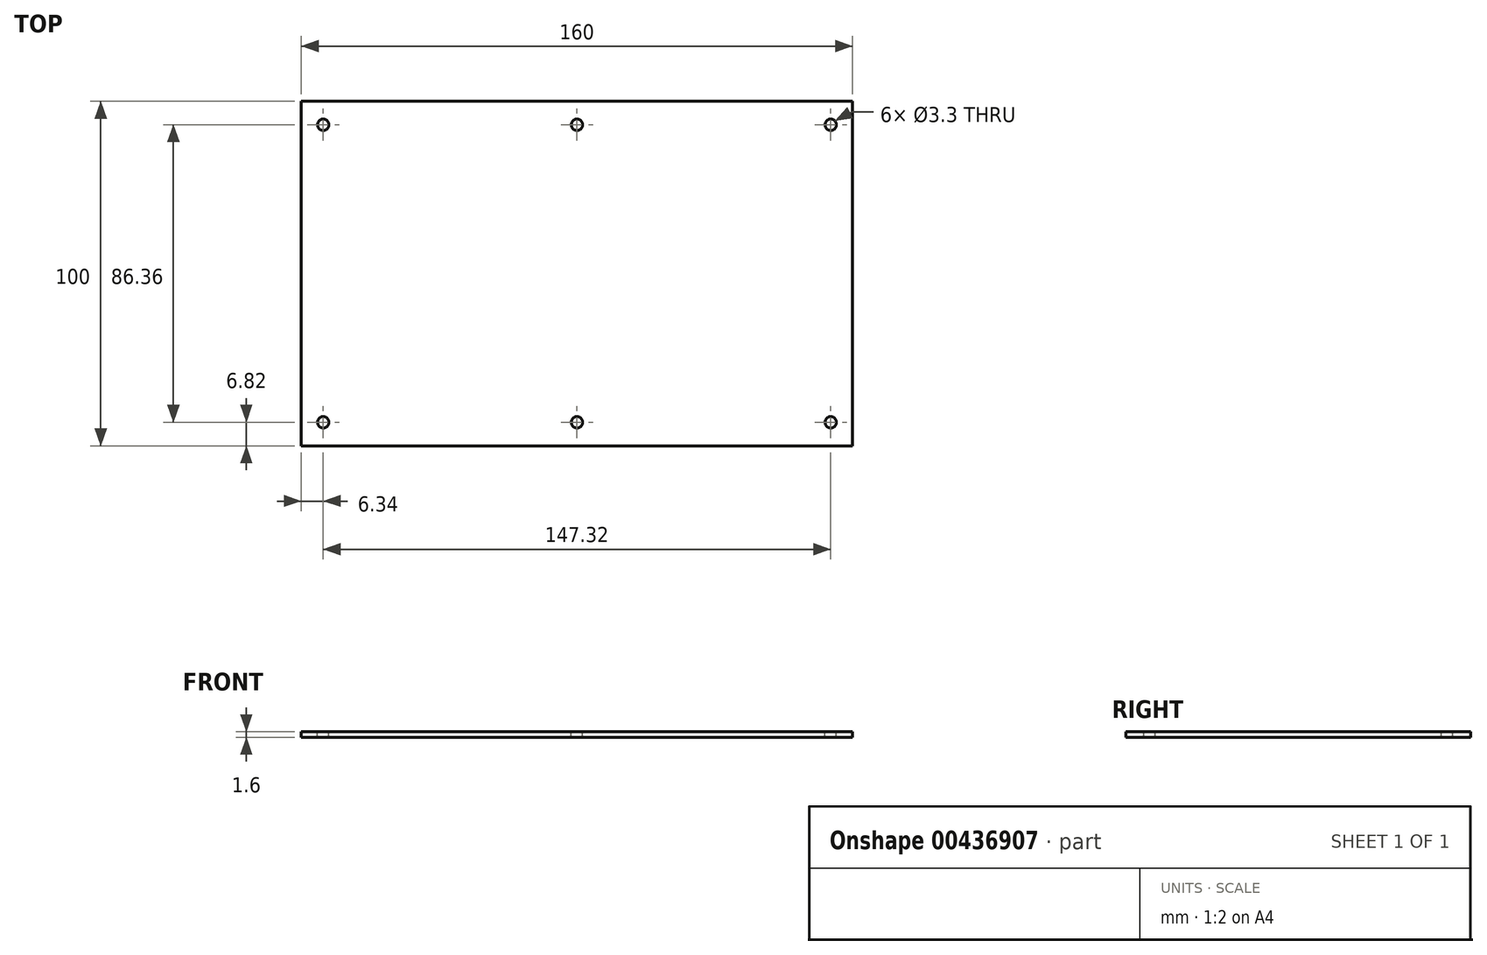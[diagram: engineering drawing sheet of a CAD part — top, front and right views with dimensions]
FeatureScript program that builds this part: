
annotation { "Feature Type Name" : "Feature", "Feature Type Description" : "" }
export const myFeature = defineFeature(function(context is Context, id is Id, definition is map)
    precondition{}
    {
        {
            var Q0;
            Q0=qCreatedBy(makeId("Top.planeOp"),FACE);
            var sketch = newSketch(context, id + "F0", { "sketchPlane" : qUnion([Q0])});
            skLineSegment(sketch, "E0.bottom", {"start": v(0, 0) * mm, "end": v(160, 0) * mm});
            skLineSegment(sketch, "E0.top", {"start": v(0, 100) * mm, "end": v(160, 100) * mm});
            skLineSegment(sketch, "E0.left", {"start": v(0, 0) * mm, "end": v(0, 100) * mm});
            skLineSegment(sketch, "E0.right", {"start": v(160, 0) * mm, "end": v(160, 100) * mm});
            skSolve(sketch);
        }
        {
            var Q0;
            Q0=qSketchRegion(id+"F0",true);
            extrude(context, id + "F1", {"entities" : qUnion([Q0]), "depth" : 1.6 * mm});
        }
        {
            var Q0;
            Q0=makeQuery(id+"F1.opExtrude","CAP_FACE",FACE,{"disambiguationData":[OSD([sQuery(id+"F0.wireOp",EDGE,"E0.bottom"),sQuery(id+"F0.wireOp",EDGE,"E0.top"),sQuery(id+"F0.wireOp",EDGE,"E0.left"),sQuery(id+"F0.wireOp",EDGE,"E0.right")])],"isStart":false});
            var sketch = newSketch(context, id + "F2", { "sketchPlane" : qUnion([Q0])});
            skPoint(sketch, "E1", {"position": v(6.34, 6.82) * mm});
            skPoint(sketch, "E2.0.1.0", {"position": v(6.34, 93.18) * mm});
            skPoint(sketch, "E2.1.0.0", {"position": v(80, 6.82) * mm});
            skPoint(sketch, "E2.1.1.0", {"position": v(80, 93.18) * mm});
            skPoint(sketch, "E2.2.0.0", {"position": v(153.66, 6.82) * mm});
            skPoint(sketch, "E2.2.1.0", {"position": v(153.66, 93.18) * mm});
            skLineSegment(sketch, "E2.direction1", {"start": v(6.34, 6.82) * mm, "end": v(80, 6.82) * mm, "construction": true});
            skLineSegment(sketch, "E2.direction2", {"start": v(6.34, 6.82) * mm, "end": v(6.34, 93.18) * mm, "construction": true});
            skSolve(sketch);
        }
        {
            var Q0;
            Q0=sQuery(id+"F2.wireOp",VERTEX,"E2.0.1.0");
            var Q1;
            Q1=sQuery(id+"F2.wireOp",VERTEX,"E1");
            var Q2;
            Q2=sQuery(id+"F2.wireOp",VERTEX,"E2.1.0.0");
            var Q3;
            Q3=sQuery(id+"F2.wireOp",VERTEX,"E2.1.1.0");
            var Q4;
            Q4=sQuery(id+"F2.wireOp",VERTEX,"E2.2.1.0");
            var Q5;
            Q5=sQuery(id+"F2.wireOp",VERTEX,"E2.2.0.0");
            var Q6;
            Q6=makeQuery(id+"F1.opExtrude","SWEPT_BODY",BODY,{"disambiguationData":[OSD([sQuery(id+"F0.wireOp",EDGE,"E0.bottom"),sQuery(id+"F0.wireOp",EDGE,"E0.top"),sQuery(id+"F0.wireOp",EDGE,"E0.left"),sQuery(id+"F0.wireOp",EDGE,"E0.right")])]});
            hole(context, id + "F3", {"style" : HoleStyle.SIMPLE, "endStyle" : HoleEndStyle.THROUGH, "standardTappedOrClearance" : lookupTablePath({ "standard" : "ISO", "fit" : "Normal", "size" : "M3", "type" : "Clearance" }), "standardBlindInLast" : lookupTablePath({ "fit" : "Standard", "standard" : "ISO", "size" : "M3", "type" : "Clearance" }), "holeDiameter" : 3.3 * mm, "isTappedThrough" : true, "tappedDepth" : 12 * mm, "tapClearance" : 3, "locations" : qUnion([Q0, Q1, Q2, Q3, Q4, Q5]), "scope" : qUnion([Q6])});
        }
    });
